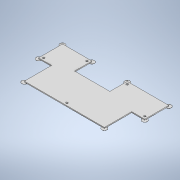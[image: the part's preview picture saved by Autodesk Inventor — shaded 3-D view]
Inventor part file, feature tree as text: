
AUTODESK INVENTOR PART (.ipt)
format: ipt  version: 2020 (Build 240168000, 168)  size: 174,592 bytes
history: native  units: mm
features: extrude x2, sketch x2, other x1
ambient origin geometry x8: Origin, YZ Plane, XZ Plane, XY Plane, X Axis, Y Axis, Z Axis, Center Point
bodies: Solid1 (feature_tree)
feature tree (5):
  other  "TopPlateV2.dwg"
  extrude  "Extrusion1"  Depth=1.5mm
  extrude  "Extrusion2"  Depth=0.2mm
  sketch  "Sketch1"  dims[d0=1.5mm d1=0.0mm d2=3.1mm]
  sketch  "Sketch2"  dims[d7=8.0mm d8=8.0mm d9=8.0mm d10=8.0mm d11=8.0mm d12=8.0mm d13=8.0mm d14=8.0mm d15=0.2mm d16=0.0mm]
